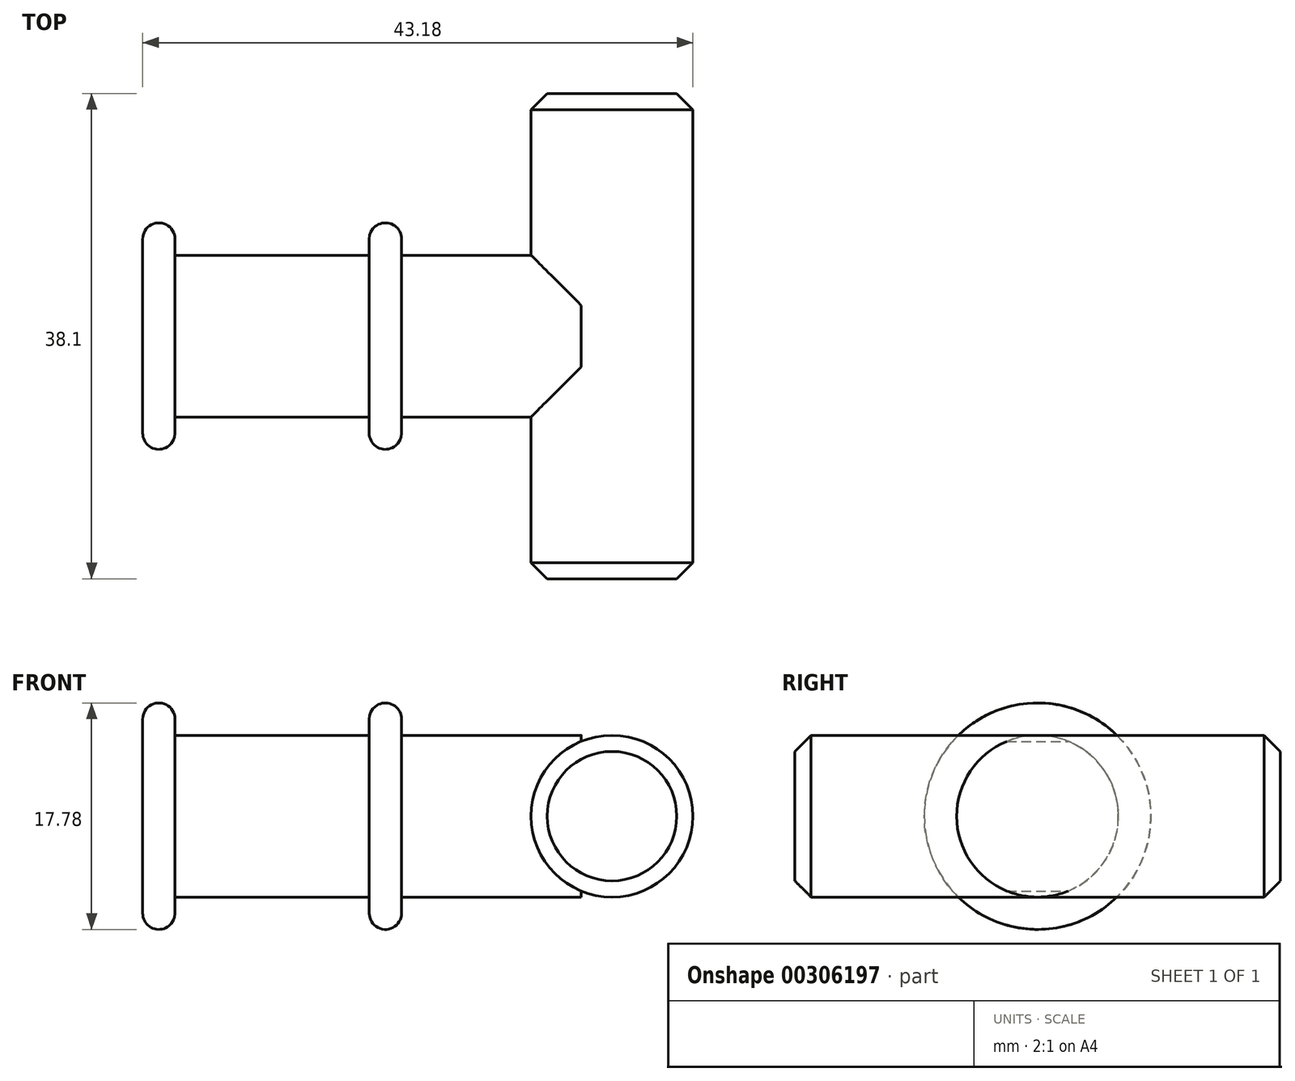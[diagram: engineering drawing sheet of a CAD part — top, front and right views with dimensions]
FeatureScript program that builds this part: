
annotation { "Feature Type Name" : "Feature", "Feature Type Description" : "" }
export const myFeature = defineFeature(function(context is Context, id is Id, definition is map)
    precondition{}
    {
        {
            var Q0;
            Q0=qCreatedBy(makeId("Right.planeOp"),FACE);
            var sketch = newSketch(context, id + "F0", { "sketchPlane" : qUnion([Q0])});
            skCircle(sketch, "E0", {"center": v(0, 182.4) * mm, "radius": 6.35 * mm});
            skSolve(sketch);
        }
        {
            var Q0;
            Q0=qSketchRegion(id+"F0",true);
            extrude(context, id + "F1", {"entities" : qUnion([Q0]), "depth" : 15.24 * mm});
        }
        {
            var Q0;
            Q0=makeQuery(id+"F1.opExtrude","CAP_FACE",FACE,{"disambiguationData":[OSD([sQuery(id+"F0.wireOp",EDGE,"E0")])],"isStart":true});
            var sketch = newSketch(context, id + "F2", { "sketchPlane" : qUnion([Q0])});
            skCircle(sketch, "E1", {"center": v(0, 182.4) * mm, "radius": 8.9 * mm});
            skSolve(sketch);
        }
        {
            var Q0;
            Q0=qSketchRegion(id+"F2",true);
            extrude(context, id + "F3", {"entities" : qUnion([Q0]), "operationType" : NewBodyOperationType.ADD, "depth" : 2.54 * mm});
        }
        {
            var Q0;
            Q0=makeQuery(id+"F3.opExtrude","SWEPT_FACE",FACE,{"disambiguationData":[OSD([sQuery(id+"F2.wireOp",EDGE,"E1")])]});
            fillet(context, id + "F4", {"entities" : qUnion([Q0]), "radius" : 1.27 * mm, "tangentPropagation" : true, "allowEdgeOverflow" : false});
        }
        {
            var Q0;
            Q0=makeQuery(id+"F1.opExtrude","CAP_FACE",FACE,{"disambiguationData":[OSD([sQuery(id+"F0.wireOp",EDGE,"E0")])],"isStart":false});
            var sketch = newSketch(context, id + "F5", { "sketchPlane" : qUnion([Q0])});
            skCircle(sketch, "E2", {"center": v(0, 182.4) * mm, "radius": 8.9 * mm});
            skSolve(sketch);
        }
        {
            var Q0;
            Q0=qSketchRegion(id+"F5",true);
            extrude(context, id + "F6", {"entities" : qUnion([Q0]), "operationType" : NewBodyOperationType.ADD, "depth" : 2.54 * mm});
        }
        {
            var Q0;
            Q0=makeQuery(id+"F6.opExtrude","SWEPT_FACE",FACE,{"disambiguationData":[OSD([sQuery(id+"F5.wireOp",EDGE,"E2")])]});
            fillet(context, id + "F7", {"entities" : qUnion([Q0]), "radius" : 1.27 * mm, "tangentPropagation" : true, "allowEdgeOverflow" : false});
        }
        {
            var Q0;
            Q0=qCreatedBy(makeId("Front.planeOp"),FACE);
            var sketch = newSketch(context, id + "F8", { "sketchPlane" : qUnion([Q0])});
            skCircle(sketch, "E3", {"center": v(34.3, 182.4) * mm, "radius": 6.35 * mm});
            skSolve(sketch);
        }
        {
            var Q0;
            Q0=qSketchRegion(id+"F8",true);
            extrude(context, id + "F9", {"entities" : qUnion([Q0]), "depth" : 38.1 * mm, "symmetric" : true});
        }
        {
            var Q0;
            Q0=makeQuery(id+"F6.opExtrude","CAP_FACE",FACE,{"disambiguationData":[OSD([sQuery(id+"F5.wireOp",EDGE,"E2")])],"isStart":false});
            var sketch = newSketch(context, id + "F10", { "sketchPlane" : qUnion([Q0])});
            skCircle(sketch, "E4", {"center": v(0, 182.4) * mm, "radius": 6.35 * mm});
            skSolve(sketch);
        }
        {
            var Q0;
            Q0=qSketchRegion(id+"F10",true);
            var Q1;
            Q1=sQuery(id+"F10.wireOp",EDGE,"E4");
            extrude(context, id + "F11", {"entities" : qUnion([Q0]), "operationType" : NewBodyOperationType.ADD, "surfaceEntities" : qUnion([Q1]), "depth" : 14.1 * mm});
        }
        {
            var Q0;
            Q0=makeQuery(id+"F9.opExtrude","CAP_EDGE",EDGE,{"disambiguationData":[OSD([sQuery(id+"F8.wireOp",EDGE,"E3")])],"isStart":false});
            var Q1;
            Q1=makeQuery(id+"F9.opExtrude","CAP_EDGE",EDGE,{"disambiguationData":[OSD([sQuery(id+"F8.wireOp",EDGE,"E3")])],"isStart":true});
            chamfer(context, id + "F12", {"entities" : qUnion([Q0, Q1]), "width" : 1.27 * mm, "tangentPropagation" : true});
        }
        {
            var Q0;
            Q0=qCreatedBy(makeId("Front.planeOp"),FACE);
            var sketch = newSketch(context, id + "F13", { "sketchPlane" : qUnion([Q0])});
            skPoint(sketch, "E5", {"position": v(15.24, 182.4) * mm});
            skLineSegment(sketch, "E6", {"start": v(15.24, 182.4) * mm, "end": v(0, 0) * mm, "construction": true});
            skSolve(sketch);
        }
        {
            var Q0;
            Q0=makeQuery(id+"F1.opExtrude","SWEPT_BODY",BODY,{"disambiguationData":[OSD([sQuery(id+"F0.wireOp",EDGE,"E0")])]});
            var Q1;
            Q1=sQuery(id+"F13.wireOp",EDGE,"E6");
            transform(context, id + "F14", {"entities" : qUnion([Q0]), "transformType" : TransformType.TRANSLATION_ENTITY, "oppositeDirectionEntity" : false, "transformLine" : qUnion([Q1]), "makeCopy" : false});
        }
    });
